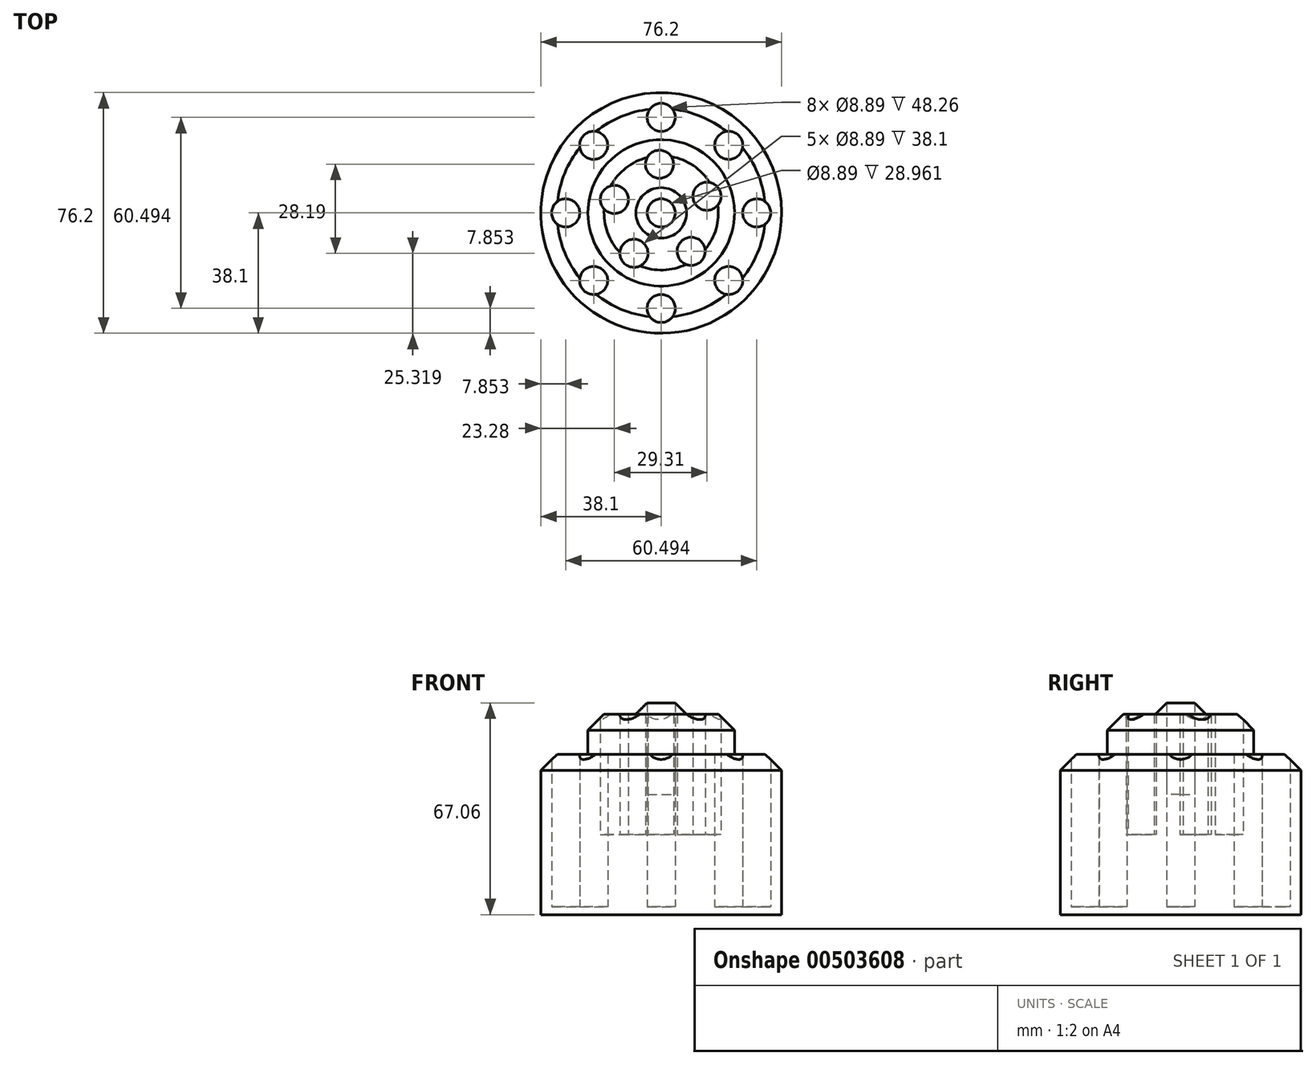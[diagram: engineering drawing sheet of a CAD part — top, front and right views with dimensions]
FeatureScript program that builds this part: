
annotation { "Feature Type Name" : "Feature", "Feature Type Description" : "" }
export const myFeature = defineFeature(function(context is Context, id is Id, definition is map)
    precondition{}
    {
        {
            var Q0;
            Q0=qCreatedBy(makeId("Top.planeOp"),FACE);
            var sketch = newSketch(context, id + "F0", { "sketchPlane" : qUnion([Q0])});
            skCircle(sketch, "E0", {"center": v(0, 0) * mm, "radius": 38.1 * mm});
            skCircle(sketch, "E1", {"center": v(0, 30.25) * mm, "radius": 4.45 * mm});
            skCircle(sketch, "E2.1.0", {"center": v(-21.39, 21.39) * mm, "radius": 4.45 * mm});
            skCircle(sketch, "E2.2.0", {"center": v(-30.25, 0) * mm, "radius": 4.45 * mm});
            skCircle(sketch, "E2.3.0", {"center": v(-21.39, -21.39) * mm, "radius": 4.45 * mm});
            skCircle(sketch, "E2.4.0", {"center": v(0, -30.25) * mm, "radius": 4.45 * mm});
            skCircle(sketch, "E2.5.0", {"center": v(21.39, -21.39) * mm, "radius": 4.45 * mm});
            skCircle(sketch, "E2.6.0", {"center": v(30.25, 0) * mm, "radius": 4.45 * mm});
            skCircle(sketch, "E2.7.0", {"center": v(21.39, 21.39) * mm, "radius": 4.45 * mm});
            skCircle(sketch, "E3", {"center": v(0, 0) * mm, "radius": 23.18 * mm});
            skCircle(sketch, "E4", {"center": v(0, 0) * mm, "radius": 4.45 * mm});
            skCircle(sketch, "E5", {"center": v(-0.54, 15.4) * mm, "radius": 4.45 * mm});
            skCircle(sketch, "E6.1.0", {"center": v(-14.82, 4.25) * mm, "radius": 4.45 * mm});
            skCircle(sketch, "E6.2.0", {"center": v(-8.62, -12.78) * mm, "radius": 4.45 * mm});
            skCircle(sketch, "E6.3.0", {"center": v(9.5, -12.15) * mm, "radius": 4.45 * mm});
            skCircle(sketch, "E6.4.0", {"center": v(14.49, 5.27) * mm, "radius": 4.45 * mm});
            skCircle(sketch, "E7", {"center": v(0, 0) * mm, "radius": 8 * mm});
            skSolve(sketch);
        }
        {
            var Q0;
            Q0=makeQuery(id+"F0.imprint","IMPRINT",FACE,{"disambiguationData":[TD([[makeQuery(id+"F0.imprint","IMPRINT",EDGE,{"derivedFrom":sQuery(id+"F0.wireOp",EDGE,"E0")}),1.0]])]});
            extrude(context, id + "F1", {"entities" : qUnion([Q0]), "depth" : 50.8 * mm});
        }
        {
            var Q0;
            Q0=makeQuery(id+"F0.imprint","IMPRINT",FACE,{"disambiguationData":[TD([[makeQuery(id+"F0.imprint","IMPRINT",EDGE,{"derivedFrom":sQuery(id+"F0.wireOp",EDGE,"E3")}),1.0]])]});
            extrude(context, id + "F2", {"entities" : qUnion([Q0]), "operationType" : NewBodyOperationType.ADD, "depth" : 63.5 * mm});
        }
        {
            var Q0;
            Q0=makeQuery(id+"F0.imprint","IMPRINT",FACE,{"disambiguationData":[TD([[makeQuery(id+"F0.imprint","IMPRINT",EDGE,{"derivedFrom":sQuery(id+"F0.wireOp",EDGE,"E4")}),-1.0]])]});
            extrude(context, id + "F3", {"entities" : qUnion([Q0]), "operationType" : NewBodyOperationType.ADD, "depth" : 68.58 * mm});
        }
        {
            var Q0;
            Q0=makeQuery(id+"F0.imprint","IMPRINT",FACE,{"disambiguationData":[TD([[makeQuery(id+"F0.imprint","IMPRINT",EDGE,{"derivedFrom":sQuery(id+"F0.wireOp",EDGE,"E2.2.0")}),1.0]])]});
            var Q1;
            Q1=makeQuery(id+"F0.imprint","IMPRINT",FACE,{"disambiguationData":[TD([[makeQuery(id+"F0.imprint","IMPRINT",EDGE,{"derivedFrom":sQuery(id+"F0.wireOp",EDGE,"E2.3.0")}),1.0]])]});
            var Q2;
            Q2=makeQuery(id+"F0.imprint","IMPRINT",FACE,{"disambiguationData":[TD([[makeQuery(id+"F0.imprint","IMPRINT",EDGE,{"derivedFrom":sQuery(id+"F0.wireOp",EDGE,"E2.4.0")}),1.0]])]});
            var Q3;
            Q3=makeQuery(id+"F0.imprint","IMPRINT",FACE,{"disambiguationData":[TD([[makeQuery(id+"F0.imprint","IMPRINT",EDGE,{"derivedFrom":sQuery(id+"F0.wireOp",EDGE,"E2.5.0")}),1.0]])]});
            var Q4;
            Q4=makeQuery(id+"F0.imprint","IMPRINT",FACE,{"disambiguationData":[TD([[makeQuery(id+"F0.imprint","IMPRINT",EDGE,{"derivedFrom":sQuery(id+"F0.wireOp",EDGE,"E2.7.0")}),1.0]])]});
            var Q5;
            Q5=makeQuery(id+"F0.imprint","IMPRINT",FACE,{"disambiguationData":[TD([[makeQuery(id+"F0.imprint","IMPRINT",EDGE,{"derivedFrom":sQuery(id+"F0.wireOp",EDGE,"E1")}),1.0]])]});
            var Q6;
            Q6=makeQuery(id+"F0.imprint","IMPRINT",FACE,{"disambiguationData":[TD([[makeQuery(id+"F0.imprint","IMPRINT",EDGE,{"derivedFrom":sQuery(id+"F0.wireOp",EDGE,"E2.1.0")}),1.0]])]});
            var Q7;
            Q7=makeQuery(id+"F0.imprint","IMPRINT",FACE,{"disambiguationData":[TD([[makeQuery(id+"F0.imprint","IMPRINT",EDGE,{"derivedFrom":sQuery(id+"F0.wireOp",EDGE,"E2.6.0")}),1.0]])]});
            extrude(context, id + "F4", {"entities" : qUnion([Q0, Q1, Q2, Q3, Q4, Q5, Q6, Q7]), "operationType" : NewBodyOperationType.ADD, "depth" : 2.54 * mm});
        }
        {
            var Q0;
            Q0=makeQuery(id+"F0.imprint","IMPRINT",FACE,{"disambiguationData":[TD([[makeQuery(id+"F0.imprint","IMPRINT",EDGE,{"derivedFrom":sQuery(id+"F0.wireOp",EDGE,"E6.2.0")}),1.0]])]});
            var Q1;
            Q1=makeQuery(id+"F0.imprint","IMPRINT",FACE,{"disambiguationData":[TD([[makeQuery(id+"F0.imprint","IMPRINT",EDGE,{"derivedFrom":sQuery(id+"F0.wireOp",EDGE,"E6.3.0")}),1.0]])]});
            var Q2;
            Q2=makeQuery(id+"F0.imprint","IMPRINT",FACE,{"disambiguationData":[TD([[makeQuery(id+"F0.imprint","IMPRINT",EDGE,{"derivedFrom":sQuery(id+"F0.wireOp",EDGE,"E6.4.0")}),1.0]])]});
            var Q3;
            Q3=makeQuery(id+"F0.imprint","IMPRINT",FACE,{"disambiguationData":[TD([[makeQuery(id+"F0.imprint","IMPRINT",EDGE,{"derivedFrom":sQuery(id+"F0.wireOp",EDGE,"E5")}),1.0]])]});
            var Q4;
            Q4=makeQuery(id+"F0.imprint","IMPRINT",FACE,{"disambiguationData":[TD([[makeQuery(id+"F0.imprint","IMPRINT",EDGE,{"derivedFrom":sQuery(id+"F0.wireOp",EDGE,"E6.1.0")}),1.0]])]});
            extrude(context, id + "F5", {"entities" : qUnion([Q0, Q1, Q2, Q3, Q4]), "operationType" : NewBodyOperationType.ADD, "depth" : 25.4 * mm});
        }
        {
            var Q0;
            Q0=makeQuery(id+"F0.imprint","IMPRINT",FACE,{"disambiguationData":[TD([[makeQuery(id+"F0.imprint","IMPRINT",EDGE,{"derivedFrom":sQuery(id+"F0.wireOp",EDGE,"E4")}),1.0]])]});
            extrude(context, id + "F6", {"entities" : qUnion([Q0]), "operationType" : NewBodyOperationType.ADD, "depth" : 38.1 * mm});
        }
        {
            var Q0;
            Q0=makeQuery(id+"F1.opExtrude","CAP_EDGE",EDGE,{"disambiguationData":[OSD([sQuery(id+"F0.wireOp",EDGE,"E0")])],"isStart":false});
            var Q1;
            Q1=makeQuery(id+"F2.opExtrude","CAP_EDGE",EDGE,{"disambiguationData":[OSD([sQuery(id+"F0.wireOp",EDGE,"E3")])],"isStart":false});
            var Q2;
            Q2=makeQuery(id+"F3.opExtrude","CAP_EDGE",EDGE,{"disambiguationData":[OSD([sQuery(id+"F0.wireOp",EDGE,"E7")])],"isStart":false});
            chamfer(context, id + "F7", {"entities" : qUnion([Q0, Q1, Q2]), "width" : 5.08 * mm, "tangentPropagation" : true});
        }
    });
